# Revit family: Laptop Tables
name_source: partatom
category: Furniture
units: mm (PartAtom-declared; Revit-internal decimal feet)

## family parameters
Always vertical = Yes
Cut with Voids When Loaded = No
OmniClass Number = 23.40.20.00
OmniClass Title = General Furniture and Specialties
Room Calculation Point = No
Shared = No
Work Plane-Based = No

## types (3) — shared parameters
Assembly Code = E2020200
Height = 650 mm  [stored 2.13255 ft]
LAPHA Plastic = Gresham - Black Plastic
LAPHA Top = Gresham - CONCRETE
LAPHAM Frame = Gresham - CHROME METAL
LAPHAM Top = Gresham - BLACK MFC
LAPST Feet = Gresham - Black Plastic
LAPST Top = Gresham - CONCRETE
Manufacturer = Gresham Office Furniture
Model = LAPTOP & UTILITY
Range = TABLES
URL = www.gof.co.uk

## per-type parameters (varying)
| type | H/A Catch | LAPHA | LAPHA Frame | LAPHAM | LAPHAM Plastic | LAPST | LAPST Frame |
| LAPHAM | Yes | No | Gresham - WHITE  METAL | Yes | Gresham - Black Plastic | No | Gresham - CHROME METAL |
| LAPHA | Yes | Yes | Gresham - WHITE  METAL | No | Gresham - CHROME METAL | No | Gresham - BLACK METAL |
| LAPST | No | No | Gresham - BLACK MFC | No | Gresham - CHROME METAL | Yes | Gresham - BLACK METAL |

note: column(s) folded — value = type name in every type: Product Code

note: [stored X ft] marks values corroborated as IEEE doubles in the binary element streams (Revit-internal decimal feet)

## geometry (parser evidence)
native form markers: Sweep x2
no freeform markers — native parametric forms only
